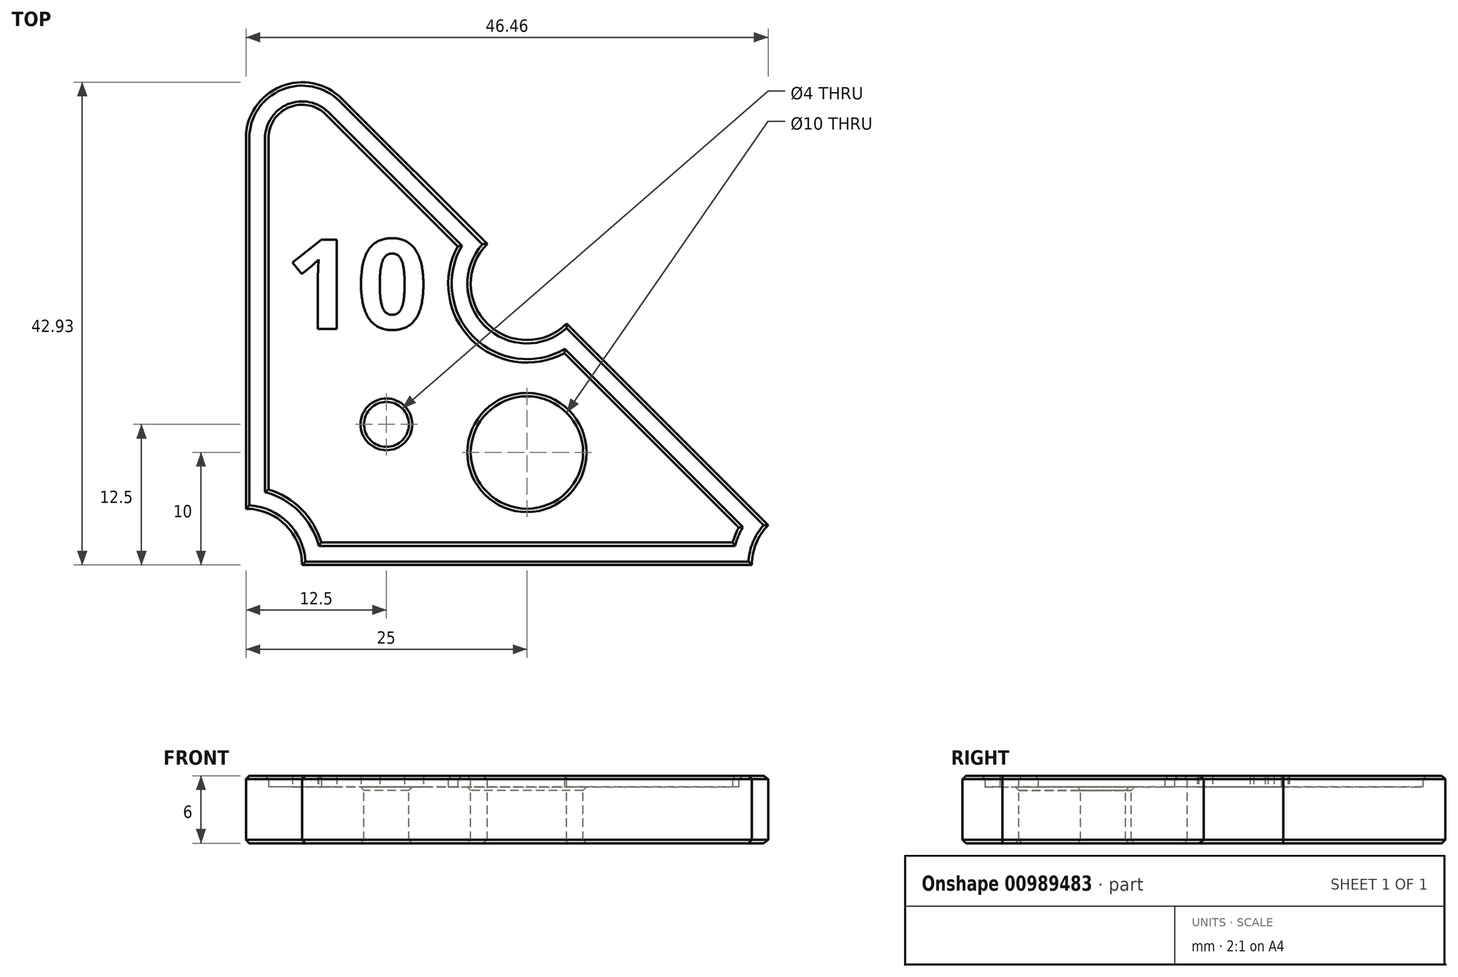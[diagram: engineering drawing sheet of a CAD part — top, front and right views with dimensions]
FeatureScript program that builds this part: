
annotation { "Feature Type Name" : "Feature", "Feature Type Description" : "" }
export const myFeature = defineFeature(function(context is Context, id is Id, definition is map)
    precondition{}
    {
        {
            var Q0;
            Q0=qCreatedBy(makeId("Top.planeOp"),FACE);
            var sketch = newSketch(context, id + "F0", { "sketchPlane" : qUnion([Q0])});
            skLineSegment(sketch, "E0", {"start": v(-25, 25) * mm, "end": v(-25, -25) * mm});
            skLineSegment(sketch, "E1", {"start": v(-25, -25) * mm, "end": v(25, -25) * mm});
            skLineSegment(sketch, "E2", {"start": v(25, -25) * mm, "end": v(-25, 25) * mm});
            skPoint(sketch, "E3", {"position": v(0, 0) * mm});
            skCircle(sketch, "E4", {"center": v(-25, -25) * mm, "radius": 5 * mm});
            skCircle(sketch, "E5", {"center": v(25, -25) * mm, "radius": 5 * mm});
            skCircle(sketch, "E6", {"center": v(0, 0) * mm, "radius": 5 * mm});
            skArc(sketch, "E7", {"start": v(-16.46, 16.46) * mm, "mid": v(-21.91, 17.55) * mm, "end": v(-25, 12.93) * mm});
            skCircle(sketch, "E8", {"center": v(-12.5, -12.5) * mm, "radius": 2 * mm});
            skLineSegment(sketch, "E9", {"start": v(0, 0) * mm, "end": v(-25, -25) * mm, "construction": true});
            skCircle(sketch, "E10", {"center": v(0, -15) * mm, "radius": 5 * mm});
            skLineSegment(sketch, "E11", {"start": v(0, -5) * mm, "end": v(0, -25) * mm, "construction": true});
            skPoint(sketch, "E11.startSnap0", {"position": v(0, -25) * mm});
            skLineSegment(sketch, "E12", {"start": v(-5, 5) * mm, "end": v(-5, -6.56) * mm, "construction": true});
            skLineSegment(sketch, "E13", {"start": v(-5, 0) * mm, "end": v(-25, 0) * mm, "construction": true});
            skText(sketch, "E14", { "text": "10", "fontName": "OpenSans-Bold.ttf"});
            skPoint(sketch, "E15", {"position": v(-15, 0) * mm});
            const initialGuessF0  = {"E14": [-0.0215, -0.004, 1, 0, 0.008]};
            skSetInitialGuess(sketch, initialGuessF0);
            skSolve(sketch);
        }
        {
            var Q0;
            {var subQ5=sQuery(id+"F0.wireOp",EDGE,"E7");Q0=makeQuery(id+"F0.imprint","IMPRINT",FACE,{"disambiguationData":[TD([[makeQuery(id+"F0.imprint","IMPRINT",EDGE,{"derivedFrom":subQ5}),1.0]])]});}
            var Q1;
            Q1=makeQuery(id+"F0.imprint","IMPRINT",FACE,{"disambiguationData":[TD([[makeQuery(id+"F0.imprint","IMPRINT",EDGE,{"derivedFrom":sQuery(id+"F0.wireOp",EDGE,"E14.sketch_text.stroke-0")}),-1.0]])]});
            var Q2;
            Q2=makeQuery(id+"F0.imprint","IMPRINT",FACE,{"disambiguationData":[TD([[makeQuery(id+"F0.imprint","IMPRINT",EDGE,{"derivedFrom":sQuery(id+"F0.wireOp",EDGE,"E14.sketch_text.stroke-10")}),-1.0]])]});
            var Q3;
            Q3=makeQuery(id+"F0.imprint","IMPRINT",FACE,{"disambiguationData":[TD([[makeQuery(id+"F0.imprint","IMPRINT",EDGE,{"derivedFrom":sQuery(id+"F0.wireOp",EDGE,"E14.sketch_text.stroke-18")}),1.0]])]});
            extrude(context, id + "F1", {"entities" : qUnion([Q0, Q1, Q2, Q3]), "oppositeDirection" : true, "depth" : 5 * mm, "offsetDistance" : 25 * mm});
        }
        {
            var Q0;
            Q0=makeQuery(id+"F1.opExtrude","CAP_FACE",FACE,{"disambiguationData":[OSD([sQuery(id+"F0.wireOp",EDGE,"E0"),sQuery(id+"F0.wireOp",EDGE,"E1"),sQuery(id+"F0.wireOp",EDGE,"E2"),sQuery(id+"F0.wireOp",EDGE,"E4"),sQuery(id+"F0.wireOp",EDGE,"E5"),sQuery(id+"F0.wireOp",EDGE,"E6"),sQuery(id+"F0.wireOp",EDGE,"E7"),sQuery(id+"F0.wireOp",EDGE,"E8"),sQuery(id+"F0.wireOp",EDGE,"E10")])],"isStart":true});
            var sketch = newSketch(context, id + "F2", { "sketchPlane" : qUnion([Q0])});
            skLineSegment(sketch, "E16.0", {"start": v(18.84, -21.67) * mm, "end": v(3.33, -6.16) * mm});
            skArc(sketch, "E16.1", {"start": v(18.3, -23) * mm, "mid": v(18.53, -22.32) * mm, "end": v(18.84, -21.67) * mm});
            skArc(sketch, "E16.2", {"start": v(3.33, -6.16) * mm, "mid": v(-4.95, -4.95) * mm, "end": v(-6.16, 3.33) * mm});
            skLineSegment(sketch, "E16.3", {"start": v(-18.3, -23) * mm, "end": v(18.3, -23) * mm});
            skLineSegment(sketch, "E16.4", {"start": v(-6.16, 3.33) * mm, "end": v(-17.88, 15.05) * mm});
            skArc(sketch, "E16.5", {"start": v(-17.88, 15.05) * mm, "mid": v(-21.15, 15.7) * mm, "end": v(-23, 12.93) * mm});
            skLineSegment(sketch, "E16.6", {"start": v(-23, 12.93) * mm, "end": v(-23, -18.3) * mm});
            skArc(sketch, "E16.7", {"start": v(-23, -18.3) * mm, "mid": v(-20.05, -20.05) * mm, "end": v(-18.3, -23) * mm});
            skSolve(sketch);
        }
        {
            var Q0;
            Q0=makeQuery(id+"F0.imprint","IMPRINT",FACE,{"disambiguationData":[TD([[makeQuery(id+"F0.imprint","IMPRINT",EDGE,{"derivedFrom":sQuery(id+"F0.wireOp",EDGE,"E14.sketch_text.stroke-0")}),-1.0]])]});
            var Q1;
            Q1=makeQuery(id+"F0.imprint","IMPRINT",FACE,{"disambiguationData":[TD([[makeQuery(id+"F0.imprint","IMPRINT",EDGE,{"derivedFrom":sQuery(id+"F0.wireOp",EDGE,"E14.sketch_text.stroke-10")}),-1.0]])]});
            var Q2;
            Q2=makeQuery(id+"F2.imprint","IMPRINT",FACE,{"disambiguationData":[TD([[makeQuery(id+"F2.imprint","IMPRINT",EDGE,{"derivedFrom":sQuery(id+"F2.wireOp",EDGE,"E16.0")}),-1.0]])]});
            extrude(context, id + "F3", {"entities" : qUnion([Q0, Q1, Q2]), "operationType" : NewBodyOperationType.ADD, "depth" : 1 * mm, "offsetDistance" : 25 * mm});
        }
        {
            var Q0;
            Q0=makeQuery(id+"F1.opExtrude","CAP_EDGE",EDGE,{"disambiguationData":[OSD([sQuery(id+"F0.wireOp",EDGE,"E8")])],"isStart":true});
            var Q1;
            Q1=makeQuery(id+"F1.opExtrude","CAP_EDGE",EDGE,{"disambiguationData":[OSD([sQuery(id+"F0.wireOp",EDGE,"E10")])],"isStart":true});
            var Q2;
            Q2=makeQuery(id+"F3.opExtrude","CAP_FACE",FACE,{"disambiguationData":[OSD([sQuery(id+"F0.wireOp",EDGE,"E0"),sQuery(id+"F0.wireOp",EDGE,"E1"),sQuery(id+"F0.wireOp",EDGE,"E2"),sQuery(id+"F0.wireOp",EDGE,"E4"),sQuery(id+"F0.wireOp",EDGE,"E5"),sQuery(id+"F0.wireOp",EDGE,"E6"),sQuery(id+"F0.wireOp",EDGE,"E7"),sQuery(id+"F2.wireOp",EDGE,"E16.0"),sQuery(id+"F2.wireOp",EDGE,"E16.1"),sQuery(id+"F2.wireOp",EDGE,"E16.2"),sQuery(id+"F2.wireOp",EDGE,"E16.3"),sQuery(id+"F2.wireOp",EDGE,"E16.4"),sQuery(id+"F2.wireOp",EDGE,"E16.5"),sQuery(id+"F2.wireOp",EDGE,"E16.6"),sQuery(id+"F2.wireOp",EDGE,"E16.7")])],"isStart":false});
            var Q3;
            Q3=makeQuery(id+"F1.opExtrude","CAP_FACE",FACE,{"disambiguationData":[OSD([sQuery(id+"F0.wireOp",EDGE,"E0"),sQuery(id+"F0.wireOp",EDGE,"E1"),sQuery(id+"F0.wireOp",EDGE,"E2"),sQuery(id+"F0.wireOp",EDGE,"E4"),sQuery(id+"F0.wireOp",EDGE,"E5"),sQuery(id+"F0.wireOp",EDGE,"E6"),sQuery(id+"F0.wireOp",EDGE,"E7"),sQuery(id+"F0.wireOp",EDGE,"E8"),sQuery(id+"F0.wireOp",EDGE,"E10")])],"isStart":false});
            chamfer(context, id + "F4", {"entities" : qUnion([Q0, Q1, Q2, Q3]), "width" : 0.3 * mm, "tangentPropagation" : true});
        }
    });
